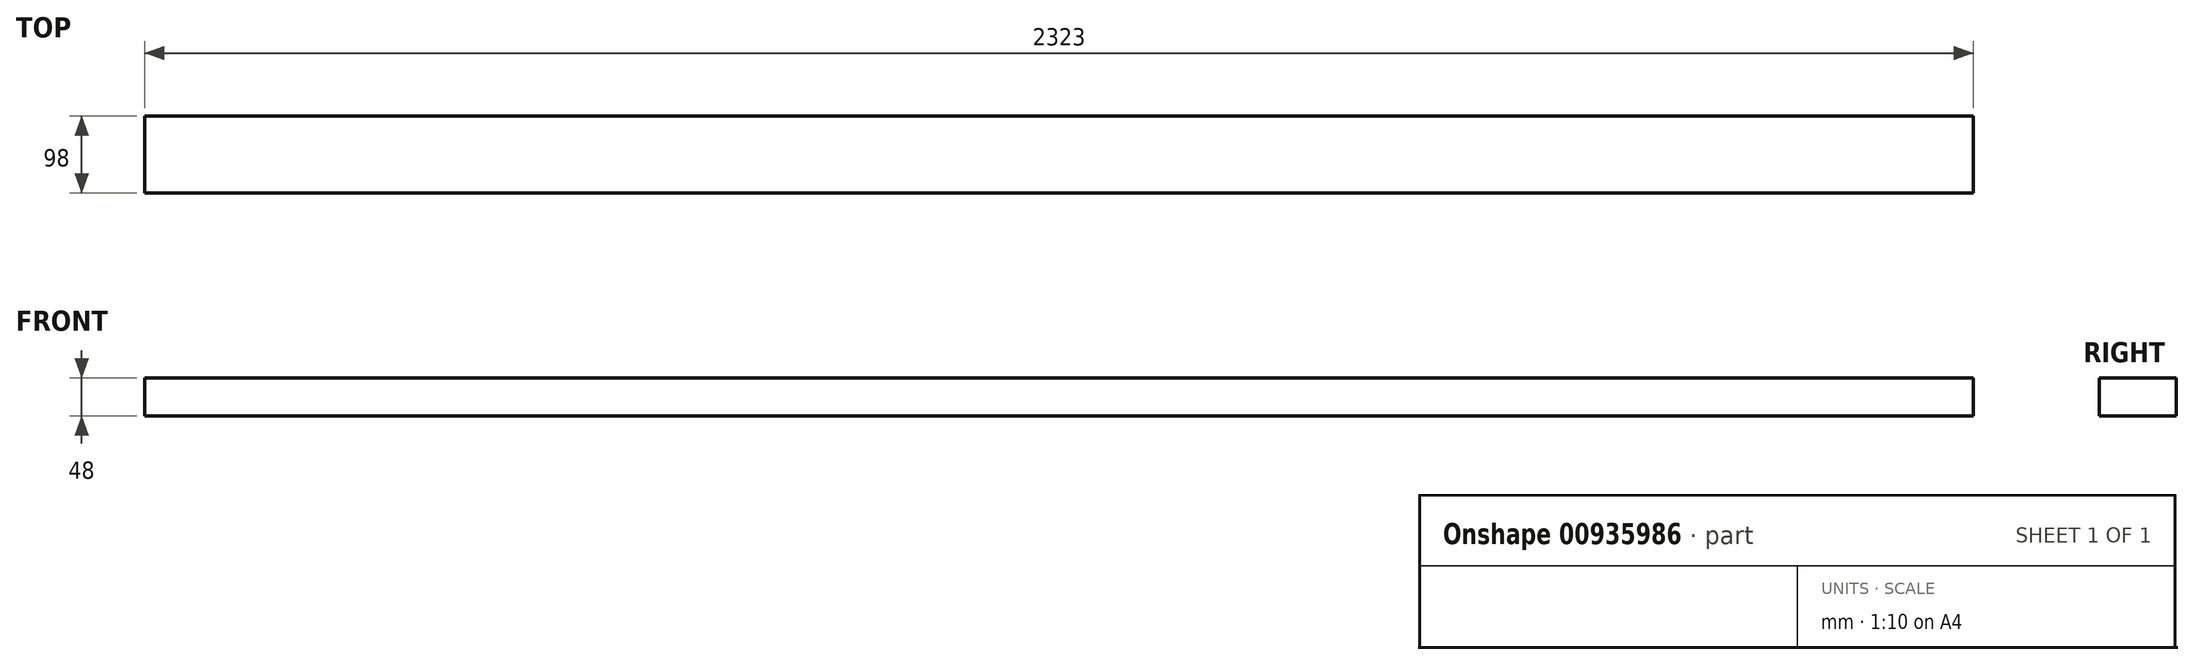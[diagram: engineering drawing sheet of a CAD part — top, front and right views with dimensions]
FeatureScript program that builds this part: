
annotation { "Feature Type Name" : "Feature", "Feature Type Description" : "" }
export const myFeature = defineFeature(function(context is Context, id is Id, definition is map)
    precondition{}
    {
        {
            var Q0;
            Q0=qCreatedBy(makeId("Right.planeOp"),FACE);
            var sketch = newSketch(context, id + "F0", { "sketchPlane" : qUnion([Q0])});
            skLineSegment(sketch, "E0.bottom", {"start": v(49, -24) * mm, "end": v(-49, -24) * mm});
            skLineSegment(sketch, "E0.top", {"start": v(49, 24) * mm, "end": v(-49, 24) * mm});
            skLineSegment(sketch, "E0.left", {"start": v(49, -24) * mm, "end": v(49, 24) * mm});
            skLineSegment(sketch, "E0.right", {"start": v(-49, -24) * mm, "end": v(-49, 24) * mm});
            skPoint(sketch, "E0.middle", {"position": v(0, 0) * mm});
            skSolve(sketch);
        }
        {
            assignVariable(context, id + "F1", {"name" : "Length", "anyValue" : 2323});
        }
        {
            var Q0;
            Q0=qSketchRegion(id+"F0",true);
            extrude(context, id + "F2", {"entities" : qUnion([Q0]), "depth" : (getVariable(context, 'Length')) * mm, "offsetDistance" : 25 * mm});
        }
    });
